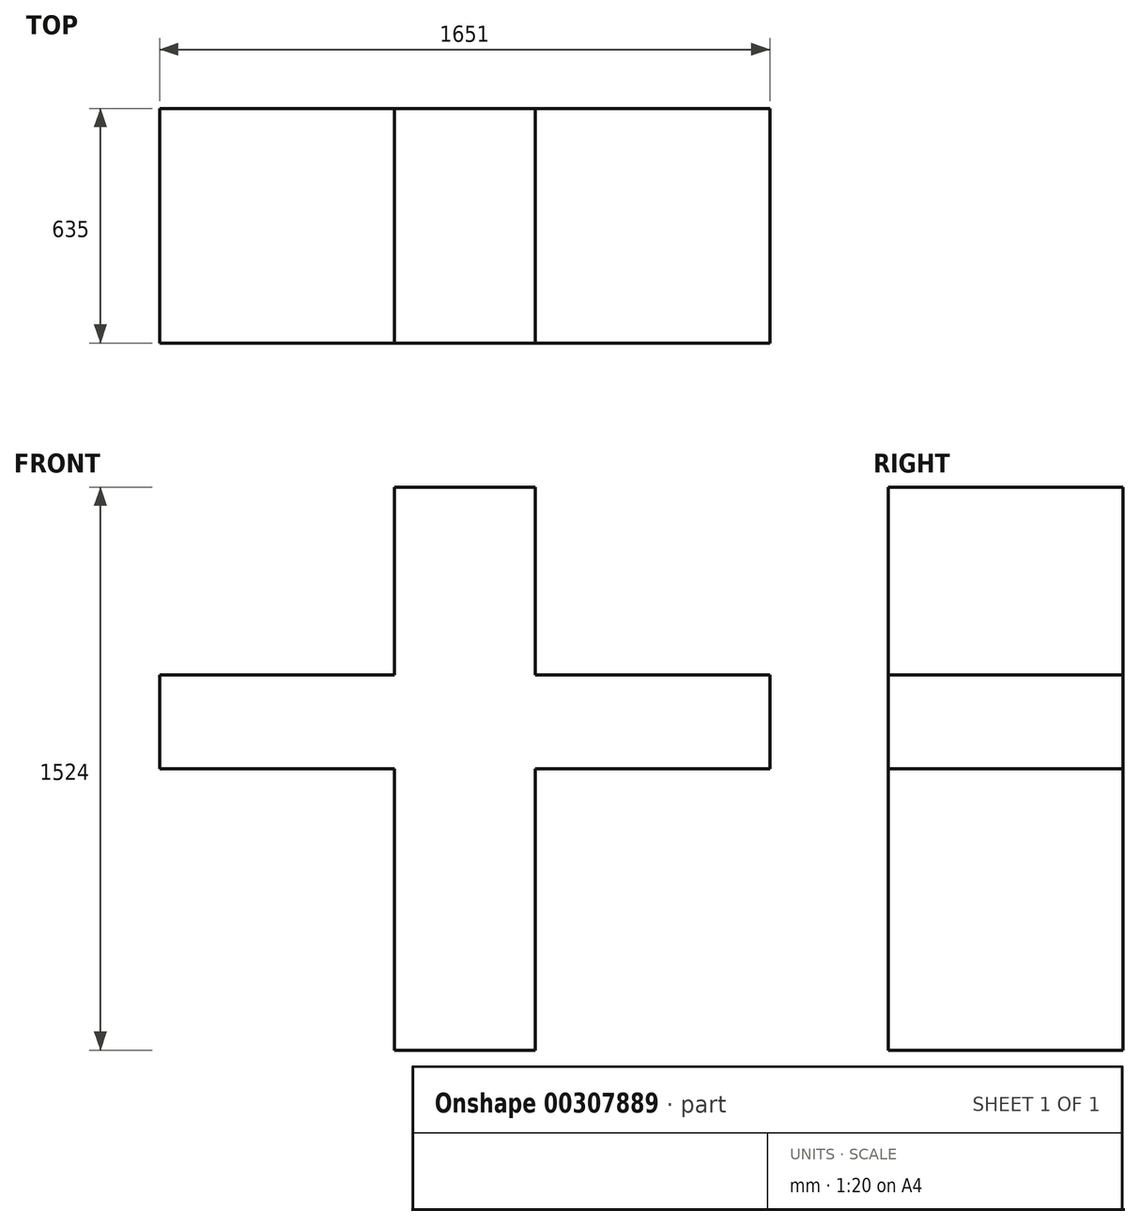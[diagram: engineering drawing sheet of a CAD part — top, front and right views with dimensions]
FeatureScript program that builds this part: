
annotation { "Feature Type Name" : "Feature", "Feature Type Description" : "" }
export const myFeature = defineFeature(function(context is Context, id is Id, definition is map)
    precondition{}
    {
        {
            var Q0;
            Q0=qCreatedBy(makeId("Front.planeOp"),FACE);
            var sketch = newSketch(context, id + "F0", { "sketchPlane" : qUnion([Q0])});
            skLineSegment(sketch, "E0", {"start": v(-225.7, 750.25) * mm, "end": v(155.3, 750.25) * mm});
            skLineSegment(sketch, "E1", {"start": v(155.3, 750.25) * mm, "end": v(155.3, 508.54) * mm});
            skLineSegment(sketch, "E2", {"start": v(155.3, 508.54) * mm, "end": v(155.3, 242.25) * mm});
            skLineSegment(sketch, "E3", {"start": v(155.3, 242.25) * mm, "end": v(790.3, 242.25) * mm});
            skLineSegment(sketch, "E4", {"start": v(790.3, 242.25) * mm, "end": v(790.3, -11.75) * mm});
            skLineSegment(sketch, "E5", {"start": v(790.3, -11.75) * mm, "end": v(155.3, -11.75) * mm});
            skLineSegment(sketch, "E6", {"start": v(155.3, -11.75) * mm, "end": v(155.3, -773.75) * mm});
            skLineSegment(sketch, "E7", {"start": v(155.3, -773.75) * mm, "end": v(-225.7, -773.75) * mm});
            skLineSegment(sketch, "E8", {"start": v(-225.7, -773.75) * mm, "end": v(-225.7, -11.75) * mm});
            skLineSegment(sketch, "E9", {"start": v(-225.7, -11.75) * mm, "end": v(-860.7, -11.75) * mm});
            skLineSegment(sketch, "E10", {"start": v(-860.7, -65.01) * mm, "end": v(-860.7, 242.25) * mm});
            skLineSegment(sketch, "E11", {"start": v(-860.7, 242.25) * mm, "end": v(-225.7, 242.25) * mm});
            skLineSegment(sketch, "E12", {"start": v(-225.7, 242.25) * mm, "end": v(-225.7, 750.25) * mm});
            skSolve(sketch);
        }
        {
            var Q0;
            Q0 = qSketchRegion(id + "F0", true);
            extrude(context, id + "F1", {"entities" : qUnion([Q0]), "depth" : 635 * mm});
        }
    });
